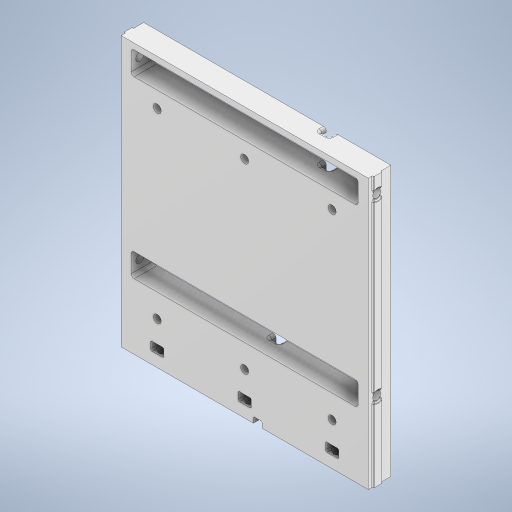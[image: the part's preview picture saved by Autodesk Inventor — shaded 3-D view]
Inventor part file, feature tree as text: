
AUTODESK INVENTOR PART (.ipt)
format: ipt  version: 2024 (Build 280153000, 153)  size: 982,016 bytes
history: native  units: mm
features: sketch x10, extrude x9, fillet x7, plane x5, projected_geometry x4, hole x3, mirror x1, chamfer x1, thicken_offset x1, other x1
ambient origin geometry x8: Origin, YZ Plane, XZ Plane, XY Plane, X Axis, Y Axis, Z Axis, Center Point
bodies: Solid1 (feature_tree)
feature tree (42):
  extrude  "Extrusion1"  Depth=185.0mm
  extrude  "Extrusion2"  Depth=9.75mm
  sketch  "Sketch3"  dims[d7=1.0mm d8=5.75mm d9=0.0mm]
  plane  "Work Plane3"
  extrude  "Extrusion3"  Depth=5.75mm TaperAngle=0.0deg
  extrude  "Extrusion4"  Depth=8.25mm
  hole  "Hole1"  [1 undecoded]
  sketch  "Sketch4"  dims[d10=120.0mm d11=8.25mm]
  plane  "Work Plane4"
  extrude  "Extrusion5"  Depth=10.0mm TaperAngle=0.0deg
  fillet  "Fillet1"  Radius=7.0mm
  hole  "Hole2"  [1 undecoded]
  extrude  "Extrusion6"  Depth=2.0mm
  mirror  "Mirror1"
  chamfer  "Chamfer1"  Distance=6.0mm
  fillet  "Fillet3"  Radius=10.0mm
  fillet  "Fillet5"  Radius=1.0mm
  fillet  "Fillet6"  Radius=9.0mm
  hole  "Hole3"  [1 undecoded]
  sketch  "Sketch9"  dims[d27=-2.0mm d28=10.0mm d29=0.0mm d30=7.0mm]
  plane  "Work Plane5"
  extrude  "Extrusion7"  Depth=0.5mm
  thicken_offset  "Thicken1"
  extrude  "Extrusion8"  Depth=0.5mm
  fillet  "Fillet7"  Radius=120.0mm
  fillet  "Fillet8"  Radius=125.0mm
  fillet  "Fillet9"  Radius=8.25mm
  sketch  "Sketch1"  dims[d0=169.6mm d1=185.0mm]
  sketch  "Sketch2"  dims[d2=5.75mm d3=9.75mm d4=0.0mm d5=0.0mm d6=5.5mm]
  plane  "Work Plane1"
  plane  "Work Plane2"
  projected_geometry  "Projected Loop1"
  sketch  "Sketch5"  dims[d12=-5.0mm d13=-3.0mm d14=-6.0mm]
  sketch  "Sketch6"  dims[d15=10.0mm d16=0.0mm d17=10.0mm d18=0.0mm]
  projected_geometry  "Projected Loop2"
  sketch  "Sketch7"  dims[d19=5.4mm d20=6.0mm d21=4.0mm d22=2.0mm d23=90.0deg d24=5.0mm d25=0.0mm]
  projected_geometry  "Projected Loop5"
  projected_geometry  "Projected Loop6"
  sketch  "Sketch10"  dims[d31=4.0mm d32=16.0mm]
  other  "Srf1"
  sketch  "Sketch11"  dims[d33=120.0mm d34=2.0mm d36=5.4mm d37=6.0mm d38=4.0mm d39=2.0mm d40=90.0deg d41=8.0mm d42=0.0mm d43=6.0mm d44=10.0mm d45=0.0mm d46=1.0mm d47=2.0mm d48=45.0deg d49=9.0mm d50=1.0mm d52=0.5mm d53=0.5mm d54=120.0mm d55=125.0mm d56=5.4mm d57=6.0mm d58=4.0mm d59=2.0mm d60=90.0deg d61=8.0mm d62=0.0mm d63=8.25mm d64=-6.0mm d65=10.0mm d66=0.0mm d67=29.0mm d73=9.0mm d74=43.5mm d75=80.0mm d76=150.0deg d77=20.0mm d78=4.0mm d79=0.0mm d80=6.0mm d81=6.0mm d82=4.0mm d83=0.0mm d84=2.0mm d85=1.0mm d86=2.0mm]
  extrude  "ExtrusionSrf1"  [1 undecoded]
note: 4 required parameter values undecoded (feature->parameter linkage not recoverable at this tier; creation-order binding heuristic only, values carry confidence <= 0.55)
